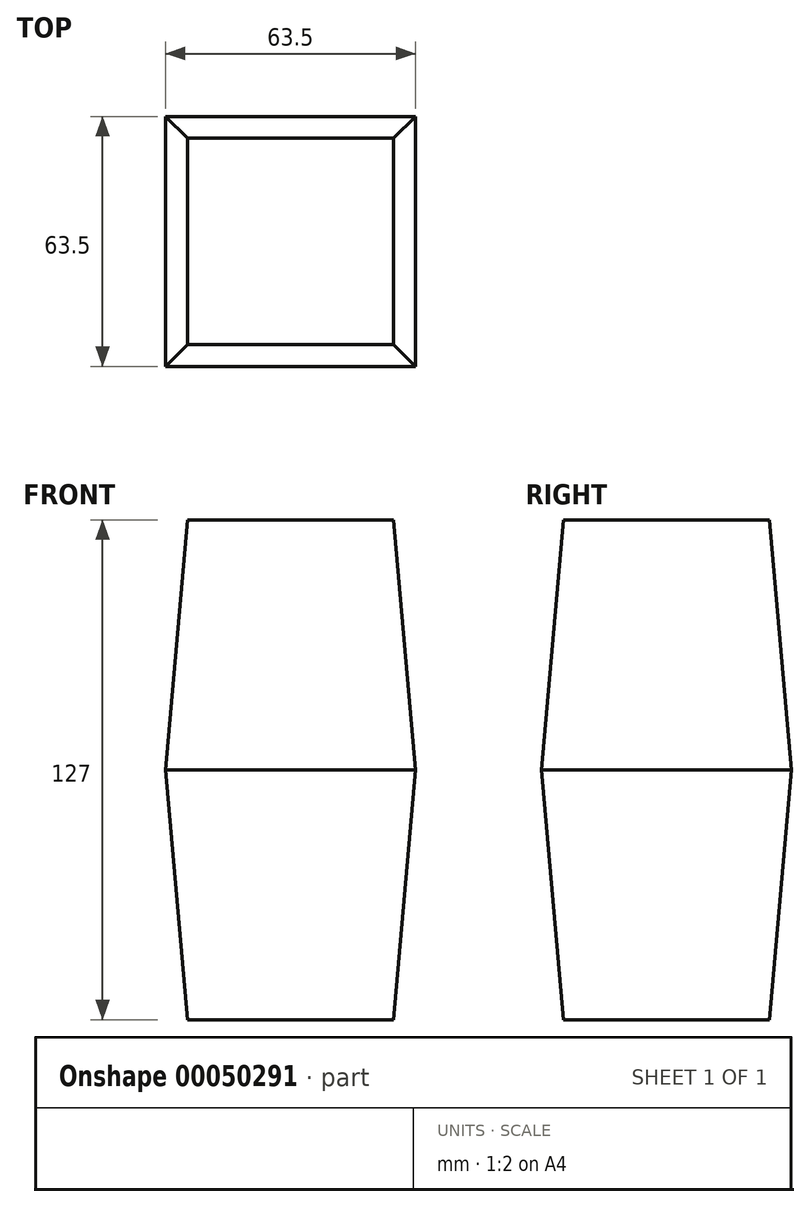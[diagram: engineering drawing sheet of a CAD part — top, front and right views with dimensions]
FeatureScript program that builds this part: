
annotation { "Feature Type Name" : "Feature", "Feature Type Description" : "" }
export const myFeature = defineFeature(function(context is Context, id is Id, definition is map)
    precondition{}
    {
        {
            var Q0;
            Q0=qCreatedBy(makeId("Top.planeOp"),FACE);
            var sketch = newSketch(context, id + "F0", { "sketchPlane" : qUnion([Q0])});
            skLineSegment(sketch, "E0.rect.bottom", {"start": v(-31.75, -31.75) * mm, "end": v(31.75, -31.75) * mm});
            skLineSegment(sketch, "E0.rect.top", {"start": v(-31.75, 31.75) * mm, "end": v(31.75, 31.75) * mm});
            skLineSegment(sketch, "E0.rect.left", {"start": v(-31.75, -31.75) * mm, "end": v(-31.75, 31.75) * mm});
            skLineSegment(sketch, "E0.rect.right", {"start": v(31.75, -31.75) * mm, "end": v(31.75, 31.75) * mm});
            skPoint(sketch, "E0.rect.middle", {"position": v(0, 0) * mm});
            skSolve(sketch);
        }
        {
            var Q0;
            Q0=makeQuery(id+"F0.imprint","IMPRINT",FACE,{"disambiguationData":[TD([[makeQuery(id+"F0.imprint","IMPRINT",EDGE,{"derivedFrom":sQuery(id+"F0.wireOp",EDGE,"E0.rect.bottom")}),1.0]])]});
            extrude(context, id + "F1", {"entities" : qUnion([Q0]), "endBound" : BoundingType.SYMMETRIC, "depth" : 127 * mm, "hasDraft" : true, "draftAngle" : 5 * degree, "draftPullDirection" : true});
        }
    });
